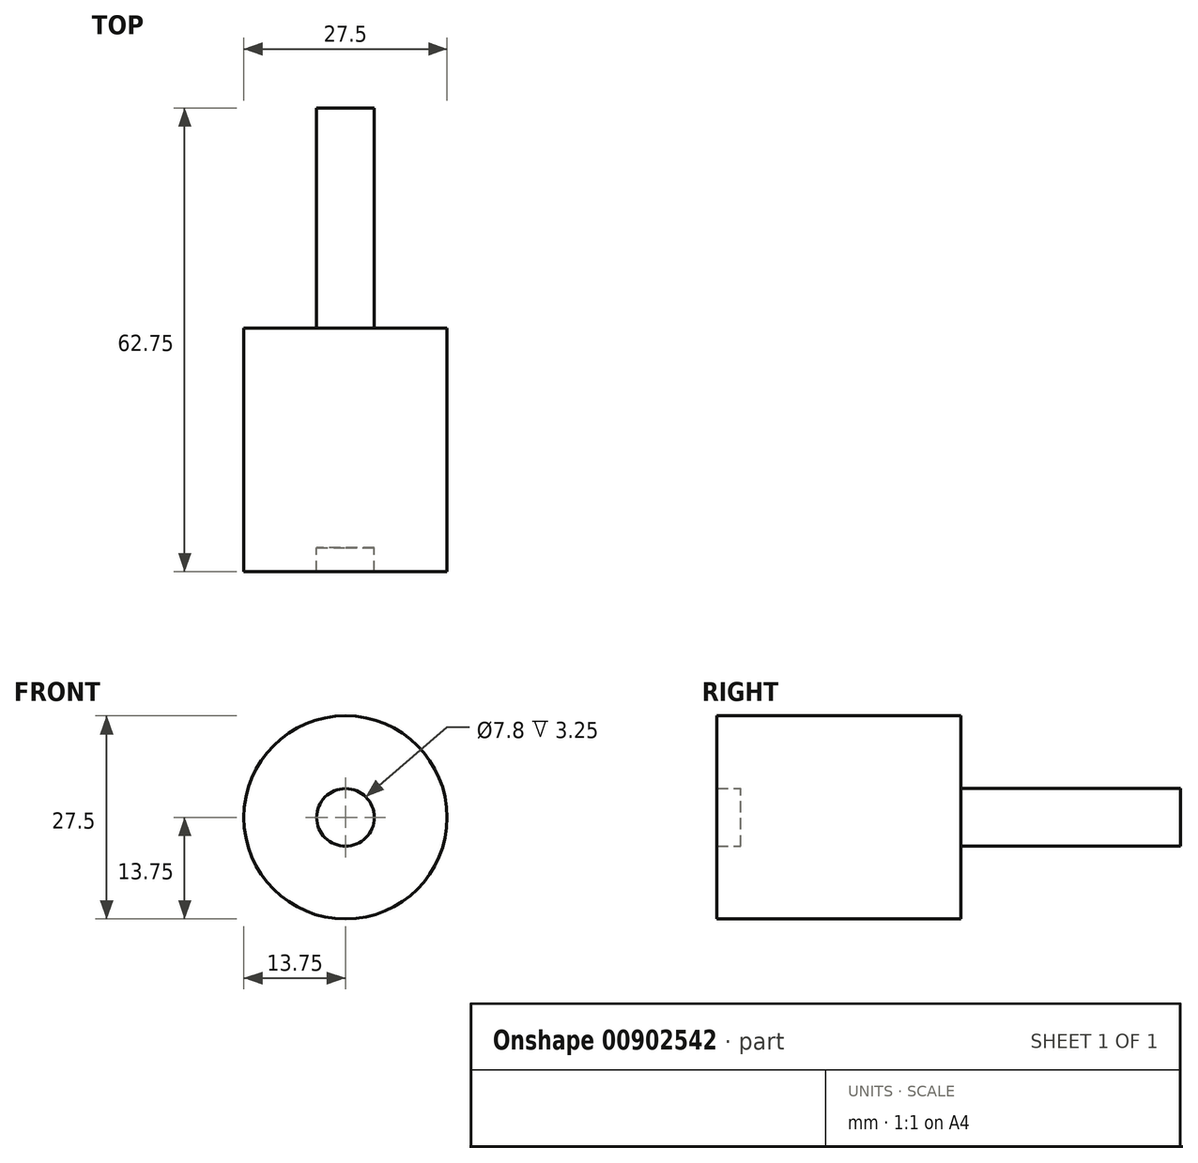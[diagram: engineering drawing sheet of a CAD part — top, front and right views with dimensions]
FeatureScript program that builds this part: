
annotation { "Feature Type Name" : "Feature", "Feature Type Description" : "" }
export const myFeature = defineFeature(function(context is Context, id is Id, definition is map)
    precondition{}
    {
        {
            var Q0;
            Q0=qCreatedBy(makeId("Front.planeOp"),FACE);
            var sketch = newSketch(context, id + "F0", { "sketchPlane" : qUnion([Q0])});
            skCircle(sketch, "E0", {"center": v(0, 0) * mm, "radius": 13.75 * mm});
            skCircle(sketch, "E1", {"center": v(0, 0) * mm, "radius": 3.9 * mm});
            skSolve(sketch);
        }
        {
            var Q0;
            Q0=makeQuery(id+"F0.imprint","IMPRINT",FACE,{"disambiguationData":[TD([[makeQuery(id+"F0.imprint","IMPRINT",EDGE,{"derivedFrom":sQuery(id+"F0.wireOp",EDGE,"E0")}),1.0]])]});
            extrude(context, id + "F1", {"entities" : qUnion([Q0]), "depth" : 33 * mm, "offsetDistance" : 25 * mm});
        }
        {
            var Q0;
            Q0=makeQuery(id+"F0.imprint","IMPRINT",FACE,{"disambiguationData":[TD([[makeQuery(id+"F0.imprint","IMPRINT",EDGE,{"derivedFrom":sQuery(id+"F0.wireOp",EDGE,"E1")}),1.0]])]});
            extrude(context, id + "F2", {"entities" : qUnion([Q0]), "operationType" : NewBodyOperationType.ADD, "oppositeDirection" : true, "depth" : 59.5 * mm, "offsetDistance" : 25 * mm, "symmetric" : true});
        }
    });
